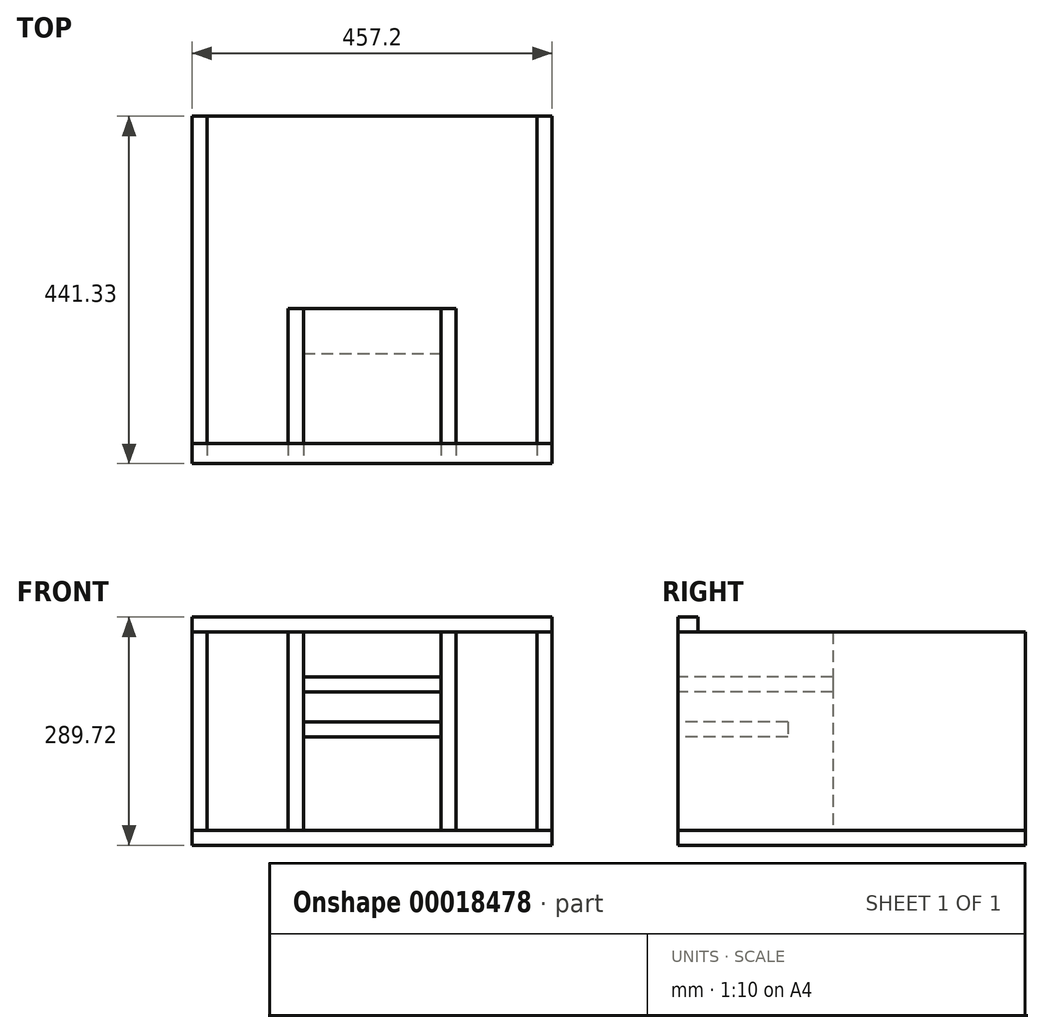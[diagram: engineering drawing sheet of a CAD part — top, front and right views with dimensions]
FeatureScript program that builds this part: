
annotation { "Feature Type Name" : "Feature", "Feature Type Description" : "" }
export const myFeature = defineFeature(function(context is Context, id is Id, definition is map)
    precondition{}
    {
        {
            var Q0;
            Q0=qCreatedBy(makeId("Front.planeOp"),FACE);
            var sketch = newSketch(context, id + "F0", { "sketchPlane" : qUnion([Q0])});
            skLineSegment(sketch, "E0.bottom", {"start": v(0, 0) * mm, "end": v(457.2, 0) * mm});
            skLineSegment(sketch, "E0.top", {"start": v(0, 289.72) * mm, "end": v(457.2, 289.72) * mm});
            skLineSegment(sketch, "E0.left", {"start": v(0, 0) * mm, "end": v(0, 289.72) * mm});
            skLineSegment(sketch, "E0.right", {"start": v(457.2, 0) * mm, "end": v(457.2, 289.72) * mm});
            skLineSegment(sketch, "E1.bottom", {"start": v(19.05, 270.67) * mm, "end": v(122.24, 270.67) * mm});
            skLineSegment(sketch, "E1.top", {"start": v(19.05, 19.05) * mm, "end": v(122.24, 19.05) * mm});
            skLineSegment(sketch, "E1.left", {"start": v(19.05, 270.67) * mm, "end": v(19.05, 19.05) * mm});
            skLineSegment(sketch, "E1.right", {"start": v(122.24, 270.67) * mm, "end": v(122.24, 19.05) * mm});
            skLineSegment(sketch, "E2.bottom", {"start": v(141.29, 19.05) * mm, "end": v(315.91, 19.05) * mm});
            skLineSegment(sketch, "E2.top", {"start": v(141.29, 137.32) * mm, "end": v(315.91, 137.32) * mm});
            skLineSegment(sketch, "E2.left", {"start": v(141.29, 19.05) * mm, "end": v(141.29, 137.32) * mm});
            skLineSegment(sketch, "E2.right", {"start": v(315.91, 19.05) * mm, "end": v(315.91, 137.32) * mm});
            skLineSegment(sketch, "E3.bottom", {"start": v(141.29, 270.67) * mm, "end": v(315.91, 270.67) * mm});
            skLineSegment(sketch, "E3.top", {"start": v(141.29, 213.52) * mm, "end": v(315.91, 213.52) * mm});
            skLineSegment(sketch, "E3.left", {"start": v(141.29, 270.67) * mm, "end": v(141.29, 213.52) * mm});
            skLineSegment(sketch, "E3.right", {"start": v(315.91, 270.67) * mm, "end": v(315.91, 213.52) * mm});
            skLineSegment(sketch, "E4.bottom", {"start": v(141.29, 194.47) * mm, "end": v(315.91, 194.47) * mm});
            skLineSegment(sketch, "E4.top", {"start": v(141.29, 156.37) * mm, "end": v(315.91, 156.37) * mm});
            skLineSegment(sketch, "E4.left", {"start": v(141.29, 194.47) * mm, "end": v(141.29, 156.37) * mm});
            skLineSegment(sketch, "E4.right", {"start": v(315.91, 194.47) * mm, "end": v(315.91, 156.37) * mm});
            skLineSegment(sketch, "E5.bottom", {"start": v(334.96, 270.67) * mm, "end": v(438.15, 270.67) * mm});
            skLineSegment(sketch, "E5.top", {"start": v(334.96, 19.05) * mm, "end": v(438.15, 19.05) * mm});
            skLineSegment(sketch, "E5.left", {"start": v(334.96, 270.67) * mm, "end": v(334.96, 19.05) * mm});
            skLineSegment(sketch, "E5.right", {"start": v(438.15, 270.67) * mm, "end": v(438.15, 19.05) * mm});
            skLineSegment(sketch, "E6", {"start": v(19.05, 270.67) * mm, "end": v(0, 270.67) * mm});
            skLineSegment(sketch, "E7", {"start": v(315.91, 270.67) * mm, "end": v(334.96, 270.67) * mm});
            skLineSegment(sketch, "E8", {"start": v(438.15, 270.67) * mm, "end": v(457.2, 270.67) * mm});
            skLineSegment(sketch, "E9", {"start": v(122.24, 270.67) * mm, "end": v(141.29, 270.67) * mm});
            skLineSegment(sketch, "E10", {"start": v(19.05, 19.05) * mm, "end": v(0, 19.05) * mm});
            skLineSegment(sketch, "E11", {"start": v(122.24, 19.05) * mm, "end": v(141.29, 19.05) * mm});
            skLineSegment(sketch, "E12", {"start": v(315.91, 19.05) * mm, "end": v(334.96, 19.05) * mm});
            skLineSegment(sketch, "E13", {"start": v(438.15, 19.05) * mm, "end": v(457.2, 19.05) * mm});
            skLineSegment(sketch, "E14", {"start": v(141.29, 213.52) * mm, "end": v(141.29, 194.47) * mm});
            skLineSegment(sketch, "E15", {"start": v(141.29, 156.37) * mm, "end": v(141.29, 137.32) * mm});
            skLineSegment(sketch, "E16", {"start": v(315.91, 213.52) * mm, "end": v(315.91, 194.47) * mm});
            skLineSegment(sketch, "E17", {"start": v(315.91, 156.37) * mm, "end": v(315.91, 137.32) * mm});
            skSolve(sketch);
        }
        {
            var Q0;
            {var subQ3=sQuery(id+"F0.wireOp",EDGE,"E0.bottom");Q0=makeQuery(id+"F0.imprint","IMPRINT",FACE,{"disambiguationData":[TD([[makeQuery(id+"F0.imprint","IMPRINT",EDGE,{"derivedFrom":subQ3}),1.0]])]});}
            extrude(context, id + "F1", {"entities" : qUnion([Q0]), "oppositeDirection" : true, "depth" : 441.32 * mm});
        }
        {
            var Q0;
            Q0=makeQuery(id+"F0.imprint","IMPRINT",FACE,{"disambiguationData":[TD([[makeQuery(id+"F0.imprint","IMPRINT",EDGE,{"derivedFrom":sQuery(id+"F0.wireOp",EDGE,"E1.left")}),-1.0]])]});
            var Q1;
            Q1=makeQuery(id+"F0.imprint","IMPRINT",FACE,{"disambiguationData":[TD([[makeQuery(id+"F0.imprint","IMPRINT",EDGE,{"derivedFrom":sQuery(id+"F0.wireOp",EDGE,"E5.right")}),1.0]])]});
            extrude(context, id + "F2", {"entities" : qUnion([Q0, Q1]), "oppositeDirection" : true, "depth" : 441.32 * mm});
        }
        {
            var Q0;
            {var subQ3=sQuery(id+"F0.wireOp",EDGE,"E0.top");Q0=makeQuery(id+"F0.imprint","IMPRINT",FACE,{"disambiguationData":[TD([[makeQuery(id+"F0.imprint","IMPRINT",EDGE,{"derivedFrom":subQ3}),-1.0]])]});}
            extrude(context, id + "F3", {"entities" : qUnion([Q0]), "oppositeDirection" : true, "depth" : 25.4 * mm});
        }
        {
            var Q0;
            Q0=makeQuery(id+"F0.imprint","IMPRINT",FACE,{"disambiguationData":[TD([[makeQuery(id+"F0.imprint","IMPRINT",EDGE,{"derivedFrom":sQuery(id+"F0.wireOp",EDGE,"E1.right")}),1.0]])]});
            var Q1;
            Q1=makeQuery(id+"F0.imprint","IMPRINT",FACE,{"disambiguationData":[TD([[makeQuery(id+"F0.imprint","IMPRINT",EDGE,{"derivedFrom":sQuery(id+"F0.wireOp",EDGE,"E2.right")}),-1.0]])]});
            extrude(context, id + "F4", {"entities" : qUnion([Q0, Q1]), "oppositeDirection" : true, "depth" : 196.85 * mm});
        }
        {
            var Q0;
            Q0=makeQuery(id+"F0.imprint","IMPRINT",FACE,{"disambiguationData":[TD([[makeQuery(id+"F0.imprint","IMPRINT",EDGE,{"derivedFrom":sQuery(id+"F0.wireOp",EDGE,"E3.top")}),-1.0]])]});
            extrude(context, id + "F5", {"entities" : qUnion([Q0]), "oppositeDirection" : true, "depth" : 196.85 * mm});
        }
        {
            var Q0;
            Q0=makeQuery(id+"F0.imprint","IMPRINT",FACE,{"disambiguationData":[TD([[makeQuery(id+"F0.imprint","IMPRINT",EDGE,{"derivedFrom":sQuery(id+"F0.wireOp",EDGE,"E2.top")}),1.0]])]});
            extrude(context, id + "F6", {"entities" : qUnion([Q0]), "oppositeDirection" : true, "depth" : 139.7 * mm});
        }
    });
